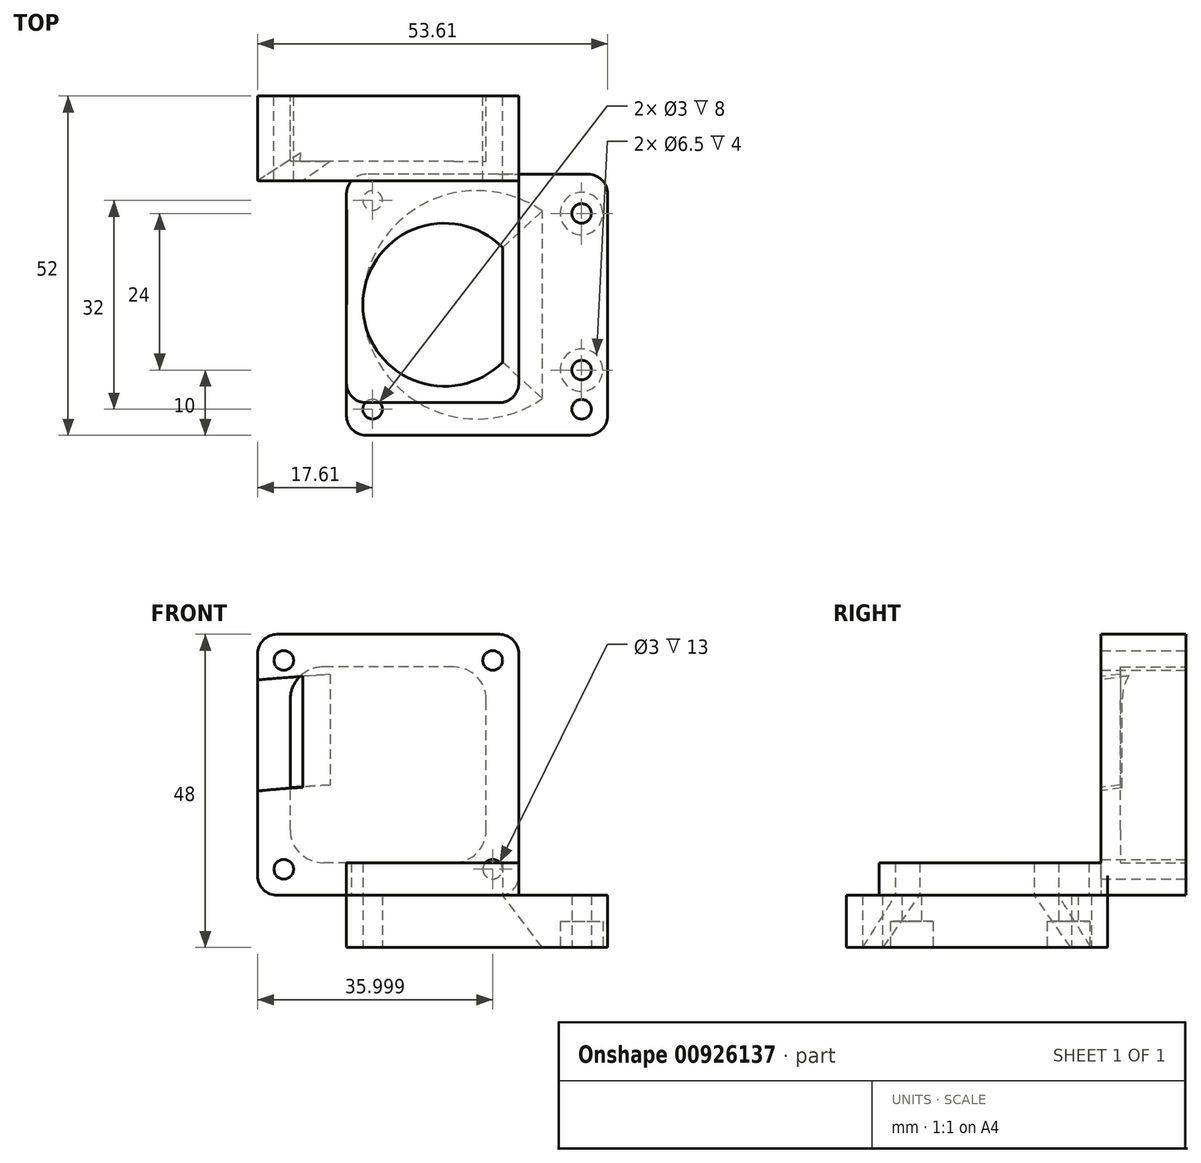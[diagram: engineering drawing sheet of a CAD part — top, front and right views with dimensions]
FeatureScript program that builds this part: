
annotation { "Feature Type Name" : "Feature", "Feature Type Description" : "" }
export const myFeature = defineFeature(function(context is Context, id is Id, definition is map)
    precondition{}
    {
        {
            var Q0;
            Q0=qCreatedBy(makeId("Top.planeOp"),FACE);
            var sketch = newSketch(context, id + "F0", { "sketchPlane" : qUnion([Q0])});
            skLineSegment(sketch, "E0.bottom", {"start": v(17, -20) * mm, "end": v(-17, -20) * mm});
            skLineSegment(sketch, "E0.top", {"start": v(17, 20) * mm, "end": v(-17, 20) * mm});
            skLineSegment(sketch, "E0.left", {"start": v(20, -17) * mm, "end": v(20, 17) * mm});
            skLineSegment(sketch, "E0.right", {"start": v(-20, -17) * mm, "end": v(-20, 17) * mm});
            skPoint(sketch, "E0.middle", {"position": v(0, 0) * mm});
            skPoint(sketch, "E1.visualSharp", {"position": v(-20, 20) * mm});
            skArc(sketch, "E1.filletArc", {"start": v(-17, 20) * mm, "mid": v(-19.12, 19.12) * mm, "end": v(-20, 17) * mm});
            skPoint(sketch, "E2.visualSharp", {"position": v(20, 20) * mm});
            skArc(sketch, "E2.filletArc", {"start": v(20, 17) * mm, "mid": v(19.12, 19.12) * mm, "end": v(17, 20) * mm});
            skPoint(sketch, "E3.visualSharp", {"position": v(-20, -20) * mm});
            skArc(sketch, "E3.filletArc", {"start": v(-20, -17) * mm, "mid": v(-19.12, -19.12) * mm, "end": v(-17, -20) * mm});
            skPoint(sketch, "E4.visualSharp", {"position": v(20, -20) * mm});
            skArc(sketch, "E4.filletArc", {"start": v(17, -20) * mm, "mid": v(19.12, -19.12) * mm, "end": v(20, -17) * mm});
            skSolve(sketch);
        }
        {
            var Q0;
            Q0=makeQuery(id+"F0.imprint","IMPRINT",FACE,{"disambiguationData":[TD([[makeQuery(id+"F0.imprint","IMPRINT",EDGE,{"derivedFrom":sQuery(id+"F0.wireOp",EDGE,"E0.bottom")}),-1.0]])]});
            extrude(context, id + "F1", {"entities" : qUnion([Q0]), "depth" : 8 * mm, "offsetDistance" : 25 * mm});
        }
        {
            var Q0;
            Q0=makeQuery(id+"F1.opExtrude","CAP_FACE",FACE,{"disambiguationData":[OSD([sQuery(id+"F0.wireOp",EDGE,"E0.bottom"),sQuery(id+"F0.wireOp",EDGE,"E0.top"),sQuery(id+"F0.wireOp",EDGE,"E0.left"),sQuery(id+"F0.wireOp",EDGE,"E0.right"),sQuery(id+"F0.wireOp",EDGE,"E1.filletArc"),sQuery(id+"F0.wireOp",EDGE,"E2.filletArc"),sQuery(id+"F0.wireOp",EDGE,"E3.filletArc"),sQuery(id+"F0.wireOp",EDGE,"E4.filletArc")])],"isStart":true});
            var sketch = newSketch(context, id + "F2", { "sketchPlane" : qUnion([Q0])});
            skCircle(sketch, "E5", {"center": v(-16, -16) * mm, "radius": 1.5 * mm});
            skCircle(sketch, "E6.0.1.0", {"center": v(-16, 16) * mm, "radius": 1.5 * mm});
            skLineSegment(sketch, "E6.direction1", {"start": v(-16, -16) * mm, "end": v(9, -16) * mm, "construction": true});
            skLineSegment(sketch, "E6.direction2", {"start": v(-16, -16) * mm, "end": v(-16, 16) * mm, "construction": true});
            skCircle(sketch, "E7.1.0.0", {"center": v(16, 16) * mm, "radius": 1.5 * mm});
            skLineSegment(sketch, "E7.direction1", {"start": v(-16, 16) * mm, "end": v(16, 16) * mm, "construction": true});
            skSolve(sketch);
        }
        {
            var Q0;
            Q0=makeQuery(id+"F2.imprint","IMPRINT",FACE,{"disambiguationData":[TD([[makeQuery(id+"F2.imprint","IMPRINT",EDGE,{"derivedFrom":sQuery(id+"F2.wireOp",EDGE,"E7.1.0.0")}),1.0]])]});
            var Q1;
            Q1=makeQuery(id+"F2.imprint","IMPRINT",FACE,{"disambiguationData":[TD([[makeQuery(id+"F2.imprint","IMPRINT",EDGE,{"derivedFrom":sQuery(id+"F2.wireOp",EDGE,"E6.0.1.0")}),1.0]])]});
            var Q2;
            Q2=makeQuery(id+"F2.imprint","IMPRINT",FACE,{"disambiguationData":[TD([[makeQuery(id+"F2.imprint","IMPRINT",EDGE,{"derivedFrom":sQuery(id+"F2.wireOp",EDGE,"E5")}),1.0]])]});
            extrude(context, id + "F3", {"entities" : qUnion([Q0, Q1, Q2]), "operationType" : NewBodyOperationType.REMOVE, "oppositeDirection" : true, "depth" : 8 * mm, "offsetDistance" : 25 * mm});
        }
        {
            var Q0;
            Q0=makeQuery(id+"F1.opExtrude","CAP_FACE",FACE,{"disambiguationData":[OSD([sQuery(id+"F0.wireOp",EDGE,"E0.bottom"),sQuery(id+"F0.wireOp",EDGE,"E0.top"),sQuery(id+"F0.wireOp",EDGE,"E0.left"),sQuery(id+"F0.wireOp",EDGE,"E0.right"),sQuery(id+"F0.wireOp",EDGE,"E1.filletArc"),sQuery(id+"F0.wireOp",EDGE,"E2.filletArc"),sQuery(id+"F0.wireOp",EDGE,"E3.filletArc"),sQuery(id+"F0.wireOp",EDGE,"E4.filletArc")])],"isStart":true});
            var sketch = newSketch(context, id + "F4", { "sketchPlane" : qUnion([Q0])});
            skCircle(sketch, "E8", {"center": v(16, -14) * mm, "radius": 3.25 * mm});
            skCircle(sketch, "E9.0.1.0", {"center": v(16, 10) * mm, "radius": 3.25 * mm});
            skLineSegment(sketch, "E9.direction1", {"start": v(16, -14) * mm, "end": v(41, -14) * mm, "construction": true});
            skLineSegment(sketch, "E9.direction2", {"start": v(16, -14) * mm, "end": v(16, 10) * mm, "construction": true});
            skSolve(sketch);
        }
        {
            var Q0;
            Q0=makeQuery(id+"F4.imprint","IMPRINT",FACE,{"disambiguationData":[TD([[makeQuery(id+"F4.imprint","IMPRINT",EDGE,{"derivedFrom":sQuery(id+"F4.wireOp",EDGE,"E9.0.1.0")}),1.0]])]});
            var Q1;
            Q1=makeQuery(id+"F4.imprint","IMPRINT",FACE,{"disambiguationData":[TD([[makeQuery(id+"F4.imprint","IMPRINT",EDGE,{"derivedFrom":sQuery(id+"F4.wireOp",EDGE,"E8")}),1.0]])]});
            extrude(context, id + "F5", {"entities" : qUnion([Q0, Q1]), "operationType" : NewBodyOperationType.REMOVE, "oppositeDirection" : true, "depth" : 4 * mm, "offsetDistance" : 25 * mm});
        }
        {
            var Q0;
            Q0=makeQuery(id+"F5.boolean.opBoolean","COPY",FACE,{"derivedFrom":makeQuery(id+"F5.opExtrude","CAP_FACE",FACE,{"disambiguationData":[OSD([sQuery(id+"F4.wireOp",EDGE,"E8")])],"isStart":false})});
            var sketch = newSketch(context, id + "F6", { "sketchPlane" : qUnion([Q0])});
            skCircle(sketch, "E10", {"center": v(16, -14) * mm, "radius": 1.5 * mm});
            skCircle(sketch, "E11.0.1.0", {"center": v(16, 10) * mm, "radius": 1.5 * mm});
            skLineSegment(sketch, "E11.direction1", {"start": v(16, -14) * mm, "end": v(41, -14) * mm, "construction": true});
            skLineSegment(sketch, "E11.direction2", {"start": v(16, -14) * mm, "end": v(16, 10) * mm, "construction": true});
            skSolve(sketch);
        }
        {
            var Q0;
            Q0=makeQuery(id+"F6.imprint","IMPRINT",FACE,{"disambiguationData":[TD([[makeQuery(id+"F6.imprint","IMPRINT",EDGE,{"derivedFrom":sQuery(id+"F6.wireOp",EDGE,"E11.0.1.0")}),1.0]])]});
            var Q1;
            Q1=makeQuery(id+"F6.imprint","IMPRINT",FACE,{"disambiguationData":[TD([[makeQuery(id+"F6.imprint","IMPRINT",EDGE,{"derivedFrom":sQuery(id+"F6.wireOp",EDGE,"E10")}),1.0]])]});
            extrude(context, id + "F7", {"entities" : qUnion([Q0, Q1]), "operationType" : NewBodyOperationType.REMOVE, "oppositeDirection" : true, "depth" : 4 * mm, "offsetDistance" : 25 * mm});
        }
        {
            var Q0;
            Q0=makeQuery(id+"F1.opExtrude","CAP_FACE",FACE,{"disambiguationData":[OSD([sQuery(id+"F0.wireOp",EDGE,"E0.bottom"),sQuery(id+"F0.wireOp",EDGE,"E0.top"),sQuery(id+"F0.wireOp",EDGE,"E0.left"),sQuery(id+"F0.wireOp",EDGE,"E0.right"),sQuery(id+"F0.wireOp",EDGE,"E1.filletArc"),sQuery(id+"F0.wireOp",EDGE,"E2.filletArc"),sQuery(id+"F0.wireOp",EDGE,"E3.filletArc"),sQuery(id+"F0.wireOp",EDGE,"E4.filletArc")])],"isStart":true});
            var sketch = newSketch(context, id + "F8", { "sketchPlane" : qUnion([Q0])});
            skCircle(sketch, "E12", {"center": v(0, 0) * mm, "radius": 17.5 * mm});
            skLineSegment(sketch, "E13", {"start": v(10, 14.36) * mm, "end": v(10, -14.36) * mm});
            skSolve(sketch);
        }
        {
            var Q0;
            Q0=makeQuery(id+"F1.opExtrude","CAP_FACE",FACE,{"disambiguationData":[OSD([sQuery(id+"F0.wireOp",EDGE,"E0.bottom"),sQuery(id+"F0.wireOp",EDGE,"E0.top"),sQuery(id+"F0.wireOp",EDGE,"E0.left"),sQuery(id+"F0.wireOp",EDGE,"E0.right"),sQuery(id+"F0.wireOp",EDGE,"E1.filletArc"),sQuery(id+"F0.wireOp",EDGE,"E2.filletArc"),sQuery(id+"F0.wireOp",EDGE,"E3.filletArc"),sQuery(id+"F0.wireOp",EDGE,"E4.filletArc")])],"isStart":false});
            var sketch = newSketch(context, id + "F9", { "sketchPlane" : qUnion([Q0])});
            skCircle(sketch, "E14", {"center": v(-5, 0) * mm, "radius": 12.5 * mm});
            skLineSegment(sketch, "E15", {"start": v(3.89, 8.79) * mm, "end": v(3.89, -8.79) * mm});
            skSolve(sketch);
        }
        {
            var Q1;
            {var subQ0=sQuery(id+"F8.wireOp",EDGE,"E13");Q1=makeQuery(id+"F8.imprint","IMPRINT",FACE,{"disambiguationData":[TD([[makeQuery(id+"F8.imprint","IMPRINT",EDGE,{"derivedFrom":subQ0}),-1.0]])]});}
            var Q2;
            {var subQ0=sQuery(id+"F9.wireOp",EDGE,"E15");Q2=makeQuery(id+"F9.imprint","IMPRINT",FACE,{"disambiguationData":[TD([[makeQuery(id+"F9.imprint","IMPRINT",EDGE,{"derivedFrom":subQ0}),-1.0]])]});}
            loft(context, id + "F10", {"operationType" : NewBodyOperationType.REMOVE, "sheetProfilesArray" : [{ "sheetProfileEntities" : qUnion([Q1]) }, { "sheetProfileEntities" : qUnion([Q2]) }]});
        }
        {
            var Q0;
            Q0=makeQuery(id+"F1.opExtrude","CAP_FACE",FACE,{"disambiguationData":[OSD([sQuery(id+"F0.wireOp",EDGE,"E0.bottom"),sQuery(id+"F0.wireOp",EDGE,"E0.top"),sQuery(id+"F0.wireOp",EDGE,"E0.left"),sQuery(id+"F0.wireOp",EDGE,"E0.right"),sQuery(id+"F0.wireOp",EDGE,"E1.filletArc"),sQuery(id+"F0.wireOp",EDGE,"E2.filletArc"),sQuery(id+"F0.wireOp",EDGE,"E3.filletArc"),sQuery(id+"F0.wireOp",EDGE,"E4.filletArc")])],"isStart":false});
            var sketch = newSketch(context, id + "F11", { "sketchPlane" : qUnion([Q0])});
            skLineSegment(sketch, "E16", {"start": v(3.89, 8.79) * mm, "end": v(3.89, -8.79) * mm});
            skArc(sketch, "E17", {"start": v(3.89, 8.79) * mm, "mid": v(-17.5, 0) * mm, "end": v(3.89, -8.79) * mm});
            skLineSegment(sketch, "E18", {"start": v(-19.99, 12) * mm, "end": v(-20, -12) * mm});
            skLineSegment(sketch, "E19", {"start": v(-17, -15) * mm, "end": v(3.39, -15) * mm});
            skLineSegment(sketch, "E20", {"start": v(6.39, -12) * mm, "end": v(6.39, 12) * mm});
            skLineSegment(sketch, "E21", {"start": v(3.39, 15) * mm, "end": v(-16.99, 15) * mm});
            skPoint(sketch, "E22.visualSharp", {"position": v(6.39, 15) * mm});
            skArc(sketch, "E22.filletArc", {"start": v(6.39, 12) * mm, "mid": v(5.51, 14.12) * mm, "end": v(3.39, 15) * mm});
            skPoint(sketch, "E23.visualSharp", {"position": v(6.39, -15) * mm});
            skArc(sketch, "E23.filletArc", {"start": v(3.39, -15) * mm, "mid": v(5.51, -14.12) * mm, "end": v(6.39, -12) * mm});
            skPoint(sketch, "E24.visualSharp", {"position": v(-20, -15) * mm});
            skArc(sketch, "E24.filletArc", {"start": v(-20, -12) * mm, "mid": v(-19.12, -14.11) * mm, "end": v(-17, -15) * mm});
            skPoint(sketch, "E25.visualSharp", {"position": v(-19.99, 15) * mm});
            skArc(sketch, "E25.filletArc", {"start": v(-16.99, 15) * mm, "mid": v(-19.1, 14.12) * mm, "end": v(-19.99, 12) * mm});
            skSolve(sketch);
        }
        {
            var Q0;
            Q0=makeQuery(id+"F11.imprint","IMPRINT",FACE,{"disambiguationData":[TD([[makeQuery(id+"F11.imprint","IMPRINT",EDGE,{"derivedFrom":sQuery(id+"F11.wireOp",EDGE,"E16")}),-1.0]])]});
            var Q1;
            {var subQ0=sQuery(id+"F11.wireOp",EDGE,"E24.filletArc");var subQ1=sQuery(id+"F11.wireOp",EDGE,"E19");var subQ2=makeQuery(id+"F11.imprint","INTERSECT",VERTEX,{"derivedFrom":[subQ1,subQ0]});Q1=makeQuery(id+"F11.imprint","IMPRINT",FACE,{"disambiguationData":[TD([[makeQuery(id+"F11.imprint","IMPRINT",EDGE,{"disambiguationData":[TD([[subQ2,-1.0]])],"derivedFrom":subQ1}),1.0]])]});}
            var Q2;
            {var subQ0=sQuery(id+"F11.wireOp",EDGE,"E25.filletArc");var subQ1=sQuery(id+"F11.wireOp",EDGE,"E21");var subQ2=makeQuery(id+"F11.imprint","INTERSECT",VERTEX,{"derivedFrom":[subQ1,subQ0]});Q2=makeQuery(id+"F11.imprint","IMPRINT",FACE,{"disambiguationData":[TD([[makeQuery(id+"F11.imprint","IMPRINT",EDGE,{"disambiguationData":[TD([[subQ2,1.0]])],"derivedFrom":subQ1}),1.0]])]});}
            extrude(context, id + "F12", {"entities" : qUnion([Q0, Q1, Q2]), "operationType" : NewBodyOperationType.ADD, "depth" : 5 * mm, "offsetDistance" : 25 * mm});
        }
        {
            var Q0;
            Q0=makeQuery(id+"F1.opExtrude","CAP_FACE",FACE,{"disambiguationData":[OSD([sQuery(id+"F0.wireOp",EDGE,"E0.bottom"),sQuery(id+"F0.wireOp",EDGE,"E0.top"),sQuery(id+"F0.wireOp",EDGE,"E0.left"),sQuery(id+"F0.wireOp",EDGE,"E0.right"),sQuery(id+"F0.wireOp",EDGE,"E1.filletArc"),sQuery(id+"F0.wireOp",EDGE,"E2.filletArc"),sQuery(id+"F0.wireOp",EDGE,"E3.filletArc"),sQuery(id+"F0.wireOp",EDGE,"E4.filletArc")])],"isStart":false});
            var sketch = newSketch(context, id + "F13", { "sketchPlane" : qUnion([Q0])});
            skPoint(sketch, "E26.orphan", {"position": v(-33.61, 12) * mm});
            skLineSegment(sketch, "E27", {"start": v(-33.61, 19) * mm, "end": v(-33.61, 32) * mm});
            skLineSegment(sketch, "E28", {"start": v(-33.61, 32) * mm, "end": v(6.39, 32) * mm});
            skLineSegment(sketch, "E29", {"start": v(6.39, 32) * mm, "end": v(6.39, 19) * mm});
            skLineSegment(sketch, "E30", {"start": v(6.39, 19) * mm, "end": v(-33.61, 19) * mm});
            skPoint(sketch, "E31.orphan", {"position": v(6.39, 15) * mm});
            skSolve(sketch);
        }
        {
            var Q0;
            {var subQ7=sQuery(id+"F13.wireOp",EDGE,"E27");Q0=makeQuery(id+"F13.imprint","IMPRINT",FACE,{"disambiguationData":[TD([[makeQuery(id+"F13.imprint","IMPRINT",EDGE,{"derivedFrom":subQ7}),-1.0]])]});}
            var Q1;
            {var subQ6=sQuery(id+"F0.wireOp",EDGE,"E1.filletArc");var subQ10=makeQuery(id+"F1.opExtrude","CAP_EDGE",EDGE,{"disambiguationData":[OSD([subQ6])],"isStart":false});Q1=makeQuery(id+"F13.imprint","IMPRINT",FACE,{"disambiguationData":[TD([[makeQuery(id+"F13.imprint","IMPRINT",EDGE,{"derivedFrom":subQ10}),1.0]])]});}
            var Q2;
            {var subQ0=sQuery(id+"F13.wireOp",EDGE,"3HEqvDyn-TJnL-be10-8rkb-lbmfub4MA3tz");var subQ1=sQuery(id+"F2.wireOp",EDGE,"E5");var subQ2=makeQuery(id+"F12.boolean.opBoolean","SPLIT",EDGE,{"disambiguationData":[topologyDisambiguationEdgeConnected([makeQuery(id+"F1.opExtrude","CAP_FACE",FACE,{"disambiguationData":[OSD([sQuery(id+"F0.wireOp",EDGE,"E0.bottom"),sQuery(id+"F0.wireOp",EDGE,"E0.top"),sQuery(id+"F0.wireOp",EDGE,"E0.left"),sQuery(id+"F0.wireOp",EDGE,"E0.right"),sQuery(id+"F0.wireOp",EDGE,"E1.filletArc"),sQuery(id+"F0.wireOp",EDGE,"E2.filletArc"),sQuery(id+"F0.wireOp",EDGE,"E3.filletArc"),sQuery(id+"F0.wireOp",EDGE,"E4.filletArc")])],"isStart":false})])],"derivedFrom":makeQuery(id+"F3.boolean.opBoolean","COPY",EDGE,{"derivedFrom":makeQuery(id+"F3.opExtrude","CAP_EDGE",EDGE,{"disambiguationData":[OSD([subQ1])],"isStart":false})})});var subQ3=makeQuery(id+"F13.imprint","INTERSECT",VERTEX,{"disambiguationData":[OD(0.0)],"derivedFrom":[subQ2,subQ0]});Q2=makeQuery(id+"F13.imprint","IMPRINT",FACE,{"disambiguationData":[TD([[makeQuery(id+"F13.imprint","IMPRINT",EDGE,{"disambiguationData":[TD([[subQ3,-1.0]])],"derivedFrom":subQ0}),-1.0]])]});}
            extrude(context, id + "F14", {"entities" : qUnion([Q0, Q1, Q2]), "operationType" : NewBodyOperationType.ADD, "depth" : 40 * mm, "offsetDistance" : 25 * mm});
        }
        {
            var Q0;
            Q0=makeQuery(id+"F1.opExtrude","CAP_FACE",FACE,{"disambiguationData":[OSD([sQuery(id+"F0.wireOp",EDGE,"E0.bottom"),sQuery(id+"F0.wireOp",EDGE,"E0.top"),sQuery(id+"F0.wireOp",EDGE,"E0.left"),sQuery(id+"F0.wireOp",EDGE,"E0.right"),sQuery(id+"F0.wireOp",EDGE,"E1.filletArc"),sQuery(id+"F0.wireOp",EDGE,"E2.filletArc"),sQuery(id+"F0.wireOp",EDGE,"E3.filletArc"),sQuery(id+"F0.wireOp",EDGE,"E4.filletArc")])],"isStart":false});
            var sketch = newSketch(context, id + "F15", { "sketchPlane" : qUnion([Q0])});
            skLineSegment(sketch, "E32", {"start": v(6.39, 12) * mm, "end": v(6.39, 19) * mm});
            skLineSegment(sketch, "E33", {"start": v(-19.99, 12) * mm, "end": v(-20, 19) * mm});
            skLineSegment(sketch, "E34", {"start": v(-19.99, 12) * mm, "end": v(-11.31, 14.67) * mm});
            skLineSegment(sketch, "E35", {"start": v(-11.31, 14.67) * mm, "end": v(6.39, 12) * mm});
            skSolve(sketch);
        }
        {
            var Q0;
            {var subQ1=sQuery(id+"F15.wireOp",EDGE,"E32");Q0=makeQuery(id+"F15.imprint","IMPRINT",FACE,{"disambiguationData":[TD([[makeQuery(id+"F15.imprint","IMPRINT",EDGE,{"derivedFrom":subQ1}),1.0]])]});}
            var Q1;
            Q1=makeQuery(id+"F15.imprint","IMPRINT",FACE,{"disambiguationData":[TD([[makeQuery(id+"F15.imprint","IMPRINT",EDGE,{"derivedFrom":sQuery(id+"F15.wireOp",EDGE,"E34")}),1.0]])]});
            extrude(context, id + "F16", {"entities" : qUnion([Q0, Q1]), "operationType" : NewBodyOperationType.ADD, "depth" : 5 * mm, "offsetDistance" : 25 * mm});
        }
        {
            var Q0;
            {var subQ0=sQuery(id+"F13.wireOp",EDGE,"E29");Q0=makeQuery(id+"F14.boolean.opBoolean","SPLIT",EDGE,{"disambiguationData":[topologyDisambiguationEdgeConnected([makeQuery(id+"F14.opExtrude","CAP_FACE",FACE,{"disambiguationData":[OSD([sQuery(id+"F13.wireOp",EDGE,"E27"),sQuery(id+"F13.wireOp",EDGE,"E28"),subQ0,sQuery(id+"F13.wireOp",EDGE,"E30")])],"isStart":true})])],"derivedFrom":makeQuery(id+"F14.opExtrude","CAP_EDGE",EDGE,{"disambiguationData":[OSD([subQ0])],"isStart":true})});}
            var Q1;
            Q1=makeQuery(id+"F14.opExtrude","CAP_EDGE",EDGE,{"disambiguationData":[OSD([sQuery(id+"F13.wireOp",EDGE,"E29")])],"isStart":false});
            var Q2;
            Q2=makeQuery(id+"F14.opExtrude","CAP_EDGE",EDGE,{"disambiguationData":[OSD([sQuery(id+"F13.wireOp",EDGE,"E27")])],"isStart":false});
            var Q3;
            Q3=makeQuery(id+"F14.opExtrude","CAP_EDGE",EDGE,{"disambiguationData":[OSD([sQuery(id+"F13.wireOp",EDGE,"E27")])],"isStart":true});
            fillet(context, id + "F17", {"entities" : qUnion([Q0, Q1, Q2, Q3]), "radius" : 3 * mm, "tangentPropagation" : true, "allowEdgeOverflow" : false});
        }
        {
            var Q0;
            Q0=makeQuery(id+"F14.opExtrude","SWEPT_FACE",FACE,{"disambiguationData":[OSD([sQuery(id+"F13.wireOp",EDGE,"E28")])]});
            var sketch = newSketch(context, id + "F18", { "sketchPlane" : qUnion([Q0])});
            skCircle(sketch, "E36", {"center": v(-2.39, 12) * mm, "radius": 1.5 * mm});
            skCircle(sketch, "E37.0.1.0", {"center": v(-2.39, 44) * mm, "radius": 1.5 * mm});
            skCircle(sketch, "E37.1.0.0", {"center": v(29.61, 12) * mm, "radius": 1.5 * mm});
            skCircle(sketch, "E37.1.1.0", {"center": v(29.61, 44) * mm, "radius": 1.5 * mm});
            skLineSegment(sketch, "E37.direction1", {"start": v(-2.39, 12) * mm, "end": v(29.61, 12) * mm, "construction": true});
            skLineSegment(sketch, "E37.direction2", {"start": v(-2.39, 12) * mm, "end": v(-2.39, 44) * mm, "construction": true});
            skSolve(sketch);
        }
        {
            var Q0;
            Q0=makeQuery(id+"F18.imprint","IMPRINT",FACE,{"disambiguationData":[TD([[makeQuery(id+"F18.imprint","IMPRINT",EDGE,{"derivedFrom":sQuery(id+"F18.wireOp",EDGE,"E36")}),1.0]])]});
            var Q1;
            Q1=makeQuery(id+"F18.imprint","IMPRINT",FACE,{"disambiguationData":[TD([[makeQuery(id+"F18.imprint","IMPRINT",EDGE,{"derivedFrom":sQuery(id+"F18.wireOp",EDGE,"E37.0.1.0")}),1.0]])]});
            var Q2;
            Q2=makeQuery(id+"F18.imprint","IMPRINT",FACE,{"disambiguationData":[TD([[makeQuery(id+"F18.imprint","IMPRINT",EDGE,{"derivedFrom":sQuery(id+"F18.wireOp",EDGE,"E37.1.1.0")}),1.0]])]});
            var Q3;
            Q3=makeQuery(id+"F18.imprint","IMPRINT",FACE,{"disambiguationData":[TD([[makeQuery(id+"F18.imprint","IMPRINT",EDGE,{"derivedFrom":sQuery(id+"F18.wireOp",EDGE,"E37.1.0.0")}),1.0]])]});
            extrude(context, id + "F19", {"entities" : qUnion([Q0, Q1, Q2, Q3]), "operationType" : NewBodyOperationType.REMOVE, "oppositeDirection" : true, "depth" : 13 * mm, "offsetDistance" : 25 * mm});
        }
        {
            var Q0;
            Q0=makeQuery(id+"F14.opExtrude","SWEPT_FACE",FACE,{"disambiguationData":[OSD([sQuery(id+"F13.wireOp",EDGE,"E28")])]});
            var sketch = newSketch(context, id + "F20", { "sketchPlane" : qUnion([Q0])});
            skLineSegment(sketch, "E38.bottom", {"start": v(3.61, 13) * mm, "end": v(23.61, 13) * mm});
            skLineSegment(sketch, "E38.top", {"start": v(3.61, 43) * mm, "end": v(23.61, 43) * mm});
            skLineSegment(sketch, "E38.left", {"start": v(-1.39, 18) * mm, "end": v(-1.39, 38) * mm});
            skLineSegment(sketch, "E38.right", {"start": v(28.61, 18) * mm, "end": v(28.61, 38) * mm});
            skPoint(sketch, "E39.visualSharp", {"position": v(-1.39, 13) * mm});
            skArc(sketch, "E39.filletArc", {"start": v(-1.39, 18) * mm, "mid": v(0.08, 14.46) * mm, "end": v(3.61, 13) * mm});
            skPoint(sketch, "E40.visualSharp", {"position": v(-1.39, 43) * mm});
            skArc(sketch, "E40.filletArc", {"start": v(3.61, 43) * mm, "mid": v(0.08, 41.54) * mm, "end": v(-1.39, 38) * mm});
            skPoint(sketch, "E41.visualSharp", {"position": v(28.61, 43) * mm});
            skArc(sketch, "E41.filletArc", {"start": v(28.61, 38) * mm, "mid": v(27.15, 41.54) * mm, "end": v(23.61, 43) * mm});
            skPoint(sketch, "E42.visualSharp", {"position": v(28.61, 13) * mm});
            skArc(sketch, "E42.filletArc", {"start": v(23.61, 13) * mm, "mid": v(27.15, 14.46) * mm, "end": v(28.61, 18) * mm});
            skSolve(sketch);
        }
        {
            var Q0;
            Q0=makeQuery(id+"F20.imprint","IMPRINT",FACE,{"disambiguationData":[TD([[makeQuery(id+"F20.imprint","IMPRINT",EDGE,{"derivedFrom":sQuery(id+"F20.wireOp",EDGE,"E38.bottom")}),1.0]])]});
            extrude(context, id + "F21", {"entities" : qUnion([Q0]), "operationType" : NewBodyOperationType.REMOVE, "oppositeDirection" : true, "depth" : 10 * mm, "offsetDistance" : 25 * mm});
        }
        {
            var Q0;
            Q0=makeQuery(id+"F14.opExtrude","SWEPT_FACE",FACE,{"disambiguationData":[OSD([sQuery(id+"F13.wireOp",EDGE,"E28")])]});
            var sketch = newSketch(context, id + "F22", { "sketchPlane" : qUnion([Q0])});
            skLineSegment(sketch, "E43.bottom", {"start": v(8.61, 26) * mm, "end": v(13.61, 26) * mm});
            skLineSegment(sketch, "E43.top", {"start": v(8.61, 43) * mm, "end": v(13.61, 43) * mm});
            skLineSegment(sketch, "E43.left", {"start": v(8.61, 26) * mm, "end": v(8.61, 43) * mm});
            skLineSegment(sketch, "E43.right", {"start": v(13.61, 26) * mm, "end": v(13.61, 43) * mm});
            skSolve(sketch);
        }
        {
            var Q0;
            Q0=makeQuery(id+"F14.opExtrude","SWEPT_FACE",FACE,{"disambiguationData":[OSD([sQuery(id+"F13.wireOp",EDGE,"E27")])]});
            var sketch = newSketch(context, id + "F23", { "sketchPlane" : qUnion([Q0])});
            skLineSegment(sketch, "E44.bottom", {"start": v(-19, 41) * mm, "end": v(-14, 41) * mm});
            skLineSegment(sketch, "E44.top", {"start": v(-19, 24) * mm, "end": v(-14, 24) * mm});
            skLineSegment(sketch, "E44.left", {"start": v(-19, 41) * mm, "end": v(-19, 24) * mm});
            skLineSegment(sketch, "E44.right", {"start": v(-14, 41) * mm, "end": v(-14, 24) * mm});
            skSolve(sketch);
        }
        {
            var Q1;
            Q1=makeQuery(id+"F22.imprint","IMPRINT",FACE,{"disambiguationData":[TD([[makeQuery(id+"F22.imprint","IMPRINT",EDGE,{"derivedFrom":sQuery(id+"F22.wireOp",EDGE,"E43.bottom")}),1.0]])]});
            var Q2;
            Q2=makeQuery(id+"F23.imprint","IMPRINT",FACE,{"disambiguationData":[TD([[makeQuery(id+"F23.imprint","IMPRINT",EDGE,{"derivedFrom":sQuery(id+"F23.wireOp",EDGE,"E44.bottom")}),-1.0]])]});
            loft(context, id + "F24", {"operationType" : NewBodyOperationType.REMOVE, "sheetProfilesArray" : [{ "sheetProfileEntities" : qUnion([Q1]) }, { "sheetProfileEntities" : qUnion([Q2]) }]});
        }
    });
